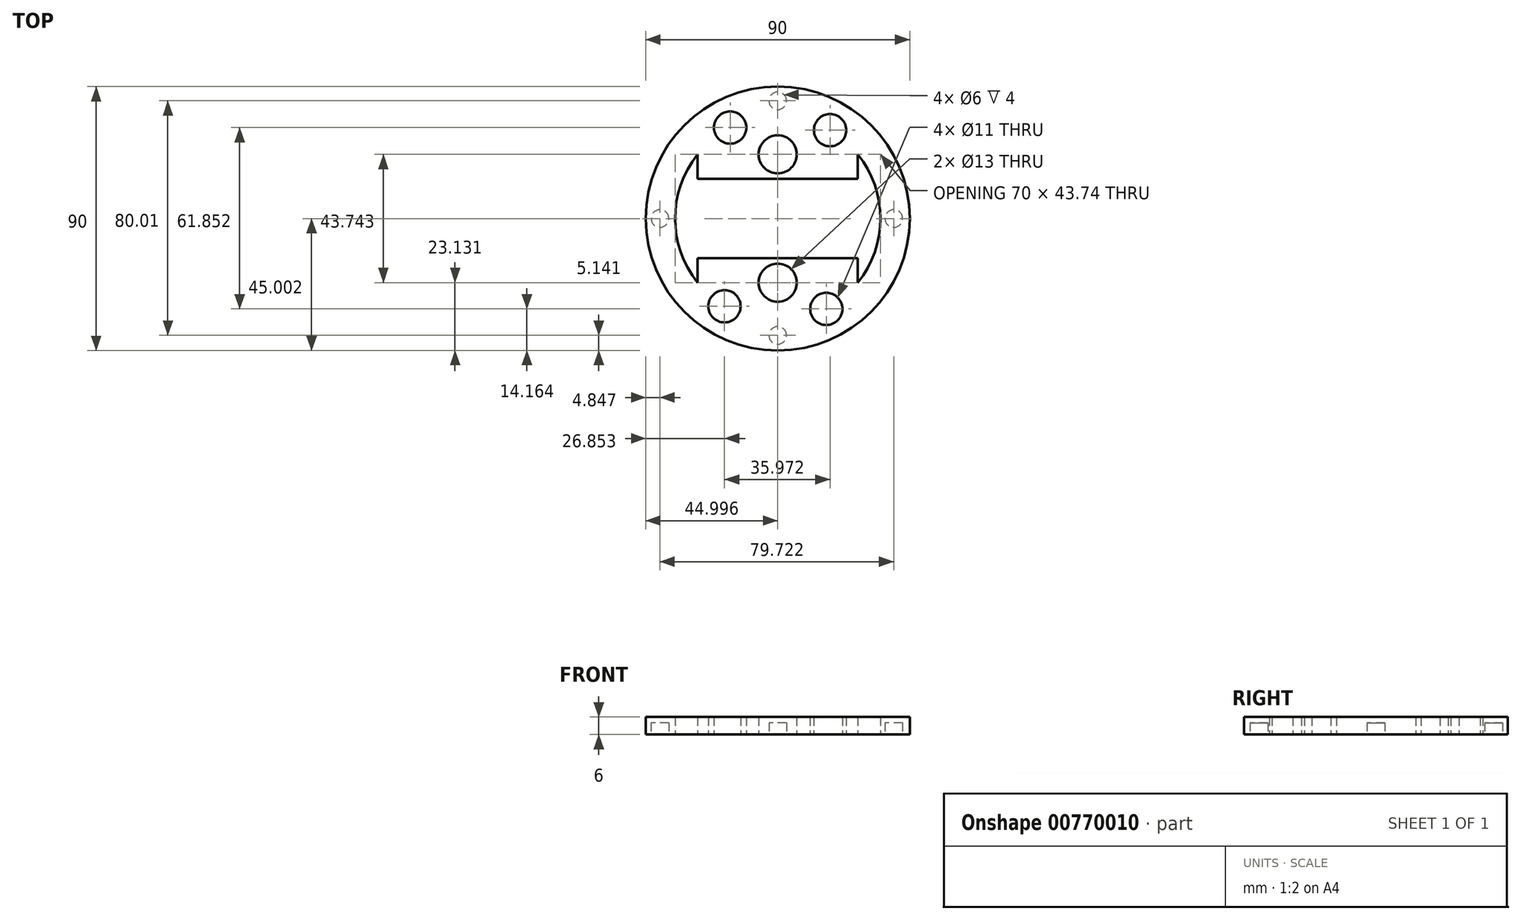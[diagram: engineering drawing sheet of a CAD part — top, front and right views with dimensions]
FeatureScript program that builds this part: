
annotation { "Feature Type Name" : "Feature", "Feature Type Description" : "" }
export const myFeature = defineFeature(function(context is Context, id is Id, definition is map)
    precondition{}
    {
        {
            var Q0;
            Q0=qCreatedBy(makeId("Top.planeOp"),FACE);
            var sketch = newSketch(context, id + "F0", { "sketchPlane" : qUnion([Q0])});
            skCircle(sketch, "E0", {"center": v(0.1, -0.05) * mm, "radius": 35 * mm});
            skCircle(sketch, "E1", {"center": v(0.1, -0.05) * mm, "radius": 45 * mm});
            skCircle(sketch, "E2", {"center": v(-40.05, -0.05) * mm, "radius": 3 * mm});
            skCircle(sketch, "E3", {"center": v(39.67, -0.05) * mm, "radius": 3 * mm});
            skCircle(sketch, "E4", {"center": v(0.1, 40.1) * mm, "radius": 3 * mm});
            skCircle(sketch, "E5", {"center": v(0.1, -39.9) * mm, "radius": 3 * mm});
            skLineSegment(sketch, "E6.bottom", {"start": v(-27.23, 21.82) * mm, "end": v(27.42, 21.82) * mm});
            skLineSegment(sketch, "E6.top", {"start": v(-27.23, -21.92) * mm, "end": v(27.42, -21.92) * mm});
            skLineSegment(sketch, "E6.left", {"start": v(-27.23, 21.82) * mm, "end": v(-27.23, -21.92) * mm});
            skLineSegment(sketch, "E6.right", {"start": v(27.42, 21.82) * mm, "end": v(27.42, -21.92) * mm});
            skCircle(sketch, "E7", {"center": v(-16.13, 30.97) * mm, "radius": 5.5 * mm});
            skCircle(sketch, "E8", {"center": v(17.92, 30.07) * mm, "radius": 5.5 * mm});
            skCircle(sketch, "E9", {"center": v(-18.05, -29.98) * mm, "radius": 5.5 * mm});
            skCircle(sketch, "E10", {"center": v(16.65, -30.89) * mm, "radius": 5.5 * mm});
            skLineSegment(sketch, "E11.bottom", {"start": v(-32.17, 13.51) * mm, "end": v(32.17, 13.51) * mm});
            skLineSegment(sketch, "E11.top", {"start": v(-32.17, -13.51) * mm, "end": v(32.17, -13.51) * mm});
            skLineSegment(sketch, "E11.left", {"start": v(-32.17, 13.51) * mm, "end": v(-32.17, -13.51) * mm});
            skLineSegment(sketch, "E11.right", {"start": v(32.17, 13.51) * mm, "end": v(32.17, -13.51) * mm});
            skPoint(sketch, "E11.middle", {"position": v(0, 0) * mm});
            skCircle(sketch, "E12", {"center": v(0.1, 21.82) * mm, "radius": 6.5 * mm});
            skCircle(sketch, "E13", {"center": v(0.1, -21.92) * mm, "radius": 6.5 * mm});
            skSolve(sketch);
        }
        {
            var Q0;
            Q0=makeQuery(id+"F0.imprint","IMPRINT",FACE,{"disambiguationData":[TD([[makeQuery(id+"F0.imprint","IMPRINT",EDGE,{"derivedFrom":sQuery(id+"F0.wireOp",EDGE,"E1")}),1.0]])]});
            var Q1;
            {var subQ0=sQuery(id+"F0.wireOp",EDGE,"E6.top");Q1=makeQuery(id+"F0.imprint","IMPRINT",FACE,{"disambiguationData":[TD([[makeQuery(id+"F0.imprint","IMPRINT",EDGE,{"derivedFrom":subQ0}),-1.0]])]});}
            var Q2;
            {var subQ0=sQuery(id+"F0.wireOp",EDGE,"E6.bottom");Q2=makeQuery(id+"F0.imprint","IMPRINT",FACE,{"disambiguationData":[TD([[makeQuery(id+"F0.imprint","IMPRINT",EDGE,{"derivedFrom":subQ0}),1.0]])]});}
            extrude(context, id + "F1", {"entities" : qUnion([Q0, Q1, Q2]), "depth" : 6 * mm, "offsetDistance" : 25 * mm});
        }
        {
            var Q0;
            {var subQ0=sQuery(id+"F0.wireOp",EDGE,"E6.bottom");Q0=makeQuery(id+"F0.imprint","IMPRINT",FACE,{"disambiguationData":[TD([[makeQuery(id+"F0.imprint","IMPRINT",EDGE,{"derivedFrom":subQ0}),-1.0]])]});}
            extrude(context, id + "F2", {"entities" : qUnion([Q0]), "operationType" : NewBodyOperationType.ADD, "depth" : 6 * mm, "offsetDistance" : 25 * mm});
        }
        {
            var Q0;
            {var subQ0=sQuery(id+"F0.wireOp",EDGE,"E6.top");Q0=makeQuery(id+"F0.imprint","IMPRINT",FACE,{"disambiguationData":[TD([[makeQuery(id+"F0.imprint","IMPRINT",EDGE,{"derivedFrom":subQ0}),1.0]])]});}
            extrude(context, id + "F3", {"entities" : qUnion([Q0]), "operationType" : NewBodyOperationType.ADD, "depth" : 6 * mm, "offsetDistance" : 25 * mm});
        }
        {
            var Q0;
            {var subQ0=sQuery(id+"F0.wireOp",EDGE,"E13");var subQ1=sQuery(id+"F0.wireOp",EDGE,"E6.right");var subQ2=sQuery(id+"F0.wireOp",EDGE,"E6.left");var subQ3=sQuery(id+"F0.wireOp",EDGE,"E6.top");var subQ4=sQuery(id+"F0.wireOp",EDGE,"E12");var subQ5=sQuery(id+"F0.wireOp",EDGE,"E6.bottom");Q0=makeQuery(id+"F3.boolean.opBoolean","MERGE",FACE,{"derivedFrom":[makeQuery(id+"F2.boolean.opBoolean","MERGE",FACE,{"derivedFrom":[makeQuery(id+"F1.opExtrude","CAP_FACE",FACE,{"disambiguationData":[OSD([sQuery(id+"F0.wireOp",EDGE,"E0"),sQuery(id+"F0.wireOp",EDGE,"E1"),sQuery(id+"F0.wireOp",EDGE,"E2"),sQuery(id+"F0.wireOp",EDGE,"E3"),sQuery(id+"F0.wireOp",EDGE,"E4"),sQuery(id+"F0.wireOp",EDGE,"E5"),subQ5,subQ3,sQuery(id+"F0.wireOp",EDGE,"E7"),sQuery(id+"F0.wireOp",EDGE,"E8"),sQuery(id+"F0.wireOp",EDGE,"E9"),sQuery(id+"F0.wireOp",EDGE,"E10"),subQ4,subQ0])],"isStart":false}),makeQuery(id+"F2.opExtrude","CAP_FACE",FACE,{"disambiguationData":[OSD([subQ5,subQ2,subQ1,sQuery(id+"F0.wireOp",EDGE,"E11.bottom"),subQ4])],"isStart":false})]}),makeQuery(id+"F3.opExtrude","CAP_FACE",FACE,{"disambiguationData":[OSD([subQ3,subQ2,subQ1,sQuery(id+"F0.wireOp",EDGE,"E11.top"),subQ0])],"isStart":false})]});}
            var sketch = newSketch(context, id + "F4", { "sketchPlane" : qUnion([Q0])});
            skCircle(sketch, "E14", {"center": v(-40.05, -0.05) * mm, "radius": 3.7 * mm});
            skCircle(sketch, "E15", {"center": v(0.1, 40.1) * mm, "radius": 3.66 * mm});
            skCircle(sketch, "E16", {"center": v(39.67, -0.05) * mm, "radius": 3.61 * mm});
            skCircle(sketch, "E17", {"center": v(0.1, -39.9) * mm, "radius": 3.82 * mm});
            skSolve(sketch);
        }
        {
            var Q0;
            Q0 = qSketchRegion(id + "F4", true);
            extrude(context, id + "F5", {"entities" : qUnion([Q0]), "operationType" : NewBodyOperationType.ADD, "oppositeDirection" : true, "depth" : 2 * mm, "offsetDistance" : 25 * mm});
        }
        {
            var Q0;
            Q0 = qSketchRegion(id + "F4", true);
            extrude(context, id + "F6", {"entities" : qUnion([Q0]), "operationType" : NewBodyOperationType.ADD, "oppositeDirection" : true, "depth" : 2 * mm, "offsetDistance" : 25 * mm});
        }
    });
